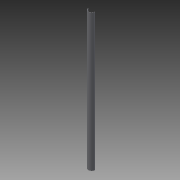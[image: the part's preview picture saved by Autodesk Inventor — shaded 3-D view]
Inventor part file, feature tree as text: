
AUTODESK INVENTOR PART (.ipt)
format: ipt  version: 2015 SP1 (Build 190203100, 203)  size: 83,968 bytes
history: native  units: mm
features: other x3, sketch x2
ambient origin geometry x8: Origin, YZ Plane, XZ Plane, XY Plane, X Axis, Y Axis, Z Axis, Center Point
bodies: Solid1 (feature_tree)
feature tree (5):
  other  "Tube sous miroir.ipt"
  other  "Solid1::Tube sous miroir.ipt"
  other  "TaggingFeature1"
  sketch  "Sketch1"  dims[d0=10.0mm]
  sketch  "Sketch2"
